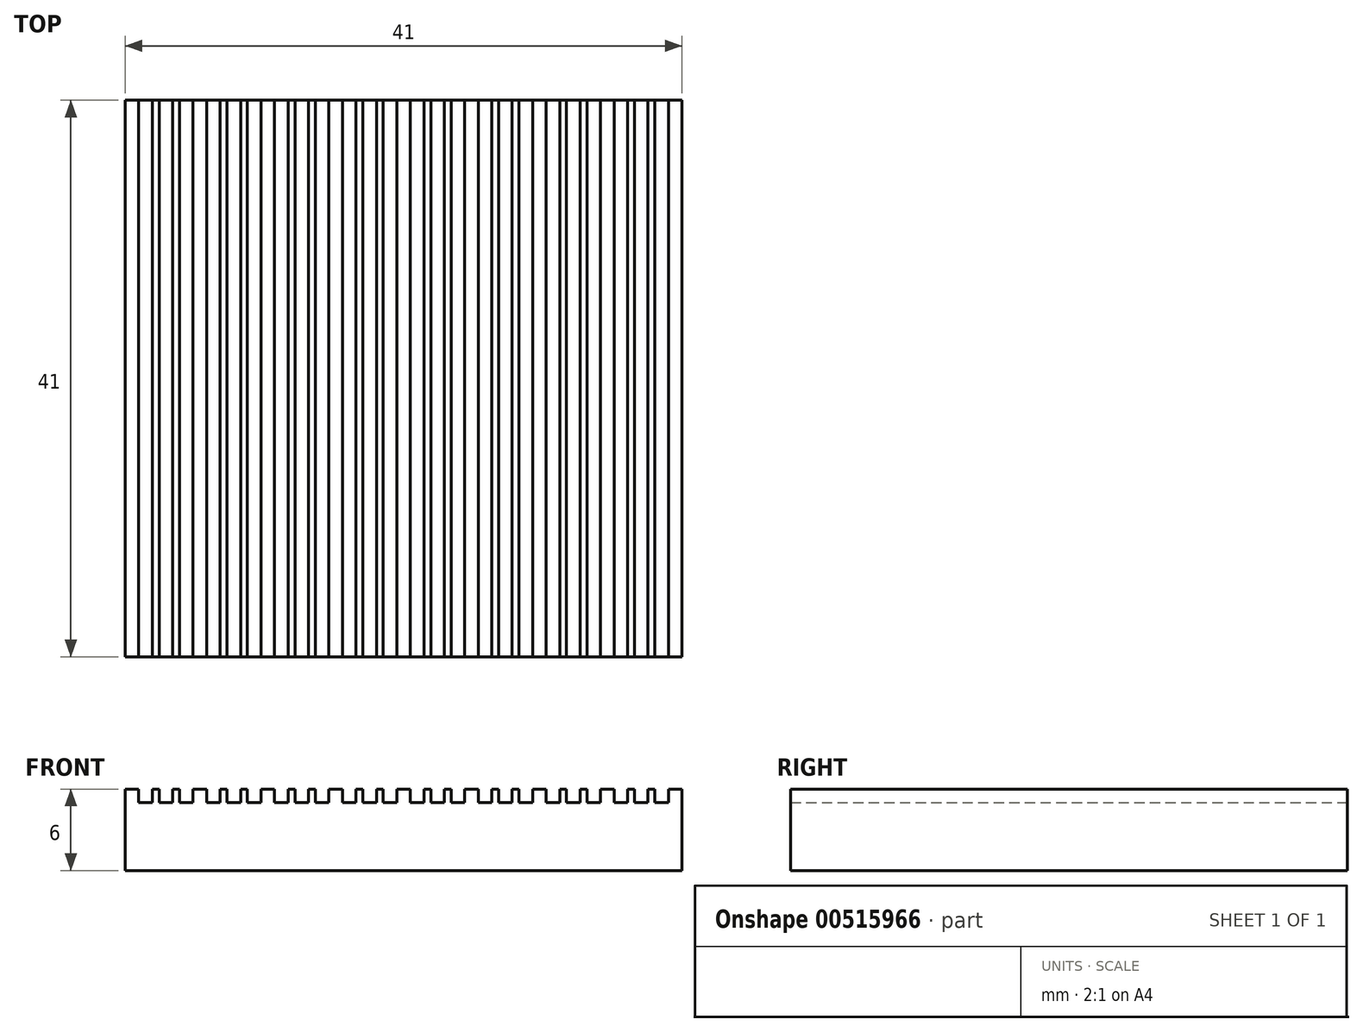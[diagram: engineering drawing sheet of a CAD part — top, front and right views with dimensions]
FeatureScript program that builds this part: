
annotation { "Feature Type Name" : "Feature", "Feature Type Description" : "" }
export const myFeature = defineFeature(function(context is Context, id is Id, definition is map)
    precondition{}
    {
        {
            var Q0;
            Q0=qCreatedBy(makeId("Front.planeOp"),FACE);
            var sketch = newSketch(context, id + "F0", { "sketchPlane" : qUnion([Q0])});
            skLineSegment(sketch, "E0", {"start": v(0, 6) * mm, "end": v(0, 0) * mm});
            skLineSegment(sketch, "E1", {"start": v(0, 0) * mm, "end": v(41, 0) * mm});
            skLineSegment(sketch, "E2", {"start": v(0, 6) * mm, "end": v(1, 6) * mm});
            skLineSegment(sketch, "E3", {"start": v(1, 6) * mm, "end": v(1, 5) * mm});
            skLineSegment(sketch, "E4", {"start": v(1, 5) * mm, "end": v(2, 5) * mm});
            skLineSegment(sketch, "E5", {"start": v(2, 5) * mm, "end": v(2, 6) * mm});
            skLineSegment(sketch, "E6", {"start": v(2, 6) * mm, "end": v(2.5, 6) * mm});
            skLineSegment(sketch, "E7", {"start": v(2.5, 6) * mm, "end": v(2.5, 5) * mm});
            skLineSegment(sketch, "E8", {"start": v(2.5, 5) * mm, "end": v(3.5, 5) * mm});
            skLineSegment(sketch, "E9", {"start": v(3.5, 5) * mm, "end": v(3.5, 6) * mm});
            skLineSegment(sketch, "E10", {"start": v(3.5, 6) * mm, "end": v(4, 6) * mm});
            skLineSegment(sketch, "E11", {"start": v(4, 6) * mm, "end": v(4, 5) * mm});
            skLineSegment(sketch, "E12", {"start": v(4, 5) * mm, "end": v(5, 5) * mm});
            skLineSegment(sketch, "E13", {"start": v(5, 5) * mm, "end": v(5, 6) * mm});
            skLineSegment(sketch, "E14.1.0.0", {"start": v(7.5, 6) * mm, "end": v(7.5, 5) * mm});
            skLineSegment(sketch, "E14.1.0.1", {"start": v(8.5, 5) * mm, "end": v(8.5, 6) * mm});
            skLineSegment(sketch, "E14.1.0.2", {"start": v(7.5, 5) * mm, "end": v(8.5, 5) * mm});
            skLineSegment(sketch, "E14.1.0.3", {"start": v(7, 5) * mm, "end": v(7, 6) * mm});
            skLineSegment(sketch, "E14.1.0.4", {"start": v(9, 6) * mm, "end": v(9, 5) * mm});
            skLineSegment(sketch, "E14.1.0.5", {"start": v(9, 5) * mm, "end": v(10, 5) * mm});
            skLineSegment(sketch, "E14.1.0.6", {"start": v(6, 5) * mm, "end": v(7, 5) * mm});
            skLineSegment(sketch, "E14.1.0.7", {"start": v(5, 6) * mm, "end": v(6, 6) * mm});
            skLineSegment(sketch, "E14.1.0.8", {"start": v(6, 6) * mm, "end": v(6, 5) * mm});
            skLineSegment(sketch, "E14.1.0.9", {"start": v(10, 5) * mm, "end": v(10, 6) * mm});
            skLineSegment(sketch, "E14.1.0.10", {"start": v(7, 6) * mm, "end": v(7.5, 6) * mm});
            skLineSegment(sketch, "E14.1.0.11", {"start": v(8.5, 6) * mm, "end": v(9, 6) * mm});
            skLineSegment(sketch, "E14.2.0.0", {"start": v(12.5, 6) * mm, "end": v(12.5, 5) * mm});
            skLineSegment(sketch, "E14.2.0.1", {"start": v(13.5, 5) * mm, "end": v(13.5, 6) * mm});
            skLineSegment(sketch, "E14.2.0.2", {"start": v(12.5, 5) * mm, "end": v(13.5, 5) * mm});
            skLineSegment(sketch, "E14.2.0.3", {"start": v(12, 5) * mm, "end": v(12, 6) * mm});
            skLineSegment(sketch, "E14.2.0.4", {"start": v(14, 6) * mm, "end": v(14, 5) * mm});
            skLineSegment(sketch, "E14.2.0.5", {"start": v(14, 5) * mm, "end": v(15, 5) * mm});
            skLineSegment(sketch, "E14.2.0.6", {"start": v(11, 5) * mm, "end": v(12, 5) * mm});
            skLineSegment(sketch, "E14.2.0.7", {"start": v(10, 6) * mm, "end": v(11, 6) * mm});
            skLineSegment(sketch, "E14.2.0.8", {"start": v(11, 6) * mm, "end": v(11, 5) * mm});
            skLineSegment(sketch, "E14.2.0.9", {"start": v(15, 5) * mm, "end": v(15, 6) * mm});
            skLineSegment(sketch, "E14.2.0.10", {"start": v(12, 6) * mm, "end": v(12.5, 6) * mm});
            skLineSegment(sketch, "E14.2.0.11", {"start": v(13.5, 6) * mm, "end": v(14, 6) * mm});
            skLineSegment(sketch, "E14.3.0.0", {"start": v(17.5, 6) * mm, "end": v(17.5, 5) * mm});
            skLineSegment(sketch, "E14.3.0.1", {"start": v(18.5, 5) * mm, "end": v(18.5, 6) * mm});
            skLineSegment(sketch, "E14.3.0.2", {"start": v(17.5, 5) * mm, "end": v(18.5, 5) * mm});
            skLineSegment(sketch, "E14.3.0.3", {"start": v(17, 5) * mm, "end": v(17, 6) * mm});
            skLineSegment(sketch, "E14.3.0.4", {"start": v(19, 6) * mm, "end": v(19, 5) * mm});
            skLineSegment(sketch, "E14.3.0.5", {"start": v(19, 5) * mm, "end": v(20, 5) * mm});
            skLineSegment(sketch, "E14.3.0.6", {"start": v(16, 5) * mm, "end": v(17, 5) * mm});
            skLineSegment(sketch, "E14.3.0.7", {"start": v(15, 6) * mm, "end": v(16, 6) * mm});
            skLineSegment(sketch, "E14.3.0.8", {"start": v(16, 6) * mm, "end": v(16, 5) * mm});
            skLineSegment(sketch, "E14.3.0.9", {"start": v(20, 5) * mm, "end": v(20, 6) * mm});
            skLineSegment(sketch, "E14.3.0.10", {"start": v(17, 6) * mm, "end": v(17.5, 6) * mm});
            skLineSegment(sketch, "E14.3.0.11", {"start": v(18.5, 6) * mm, "end": v(19, 6) * mm});
            skLineSegment(sketch, "E14.4.0.0", {"start": v(22.5, 6) * mm, "end": v(22.5, 5) * mm});
            skLineSegment(sketch, "E14.4.0.1", {"start": v(23.5, 5) * mm, "end": v(23.5, 6) * mm});
            skLineSegment(sketch, "E14.4.0.2", {"start": v(22.5, 5) * mm, "end": v(23.5, 5) * mm});
            skLineSegment(sketch, "E14.4.0.3", {"start": v(22, 5) * mm, "end": v(22, 6) * mm});
            skLineSegment(sketch, "E14.4.0.4", {"start": v(24, 6) * mm, "end": v(24, 5) * mm});
            skLineSegment(sketch, "E14.4.0.5", {"start": v(24, 5) * mm, "end": v(25, 5) * mm});
            skLineSegment(sketch, "E14.4.0.6", {"start": v(21, 5) * mm, "end": v(22, 5) * mm});
            skLineSegment(sketch, "E14.4.0.7", {"start": v(20, 6) * mm, "end": v(21, 6) * mm});
            skLineSegment(sketch, "E14.4.0.8", {"start": v(21, 6) * mm, "end": v(21, 5) * mm});
            skLineSegment(sketch, "E14.4.0.9", {"start": v(25, 5) * mm, "end": v(25, 6) * mm});
            skLineSegment(sketch, "E14.4.0.10", {"start": v(22, 6) * mm, "end": v(22.5, 6) * mm});
            skLineSegment(sketch, "E14.4.0.11", {"start": v(23.5, 6) * mm, "end": v(24, 6) * mm});
            skLineSegment(sketch, "E14.5.0.0", {"start": v(27.5, 6) * mm, "end": v(27.5, 5) * mm});
            skLineSegment(sketch, "E14.5.0.1", {"start": v(28.5, 5) * mm, "end": v(28.5, 6) * mm});
            skLineSegment(sketch, "E14.5.0.2", {"start": v(27.5, 5) * mm, "end": v(28.5, 5) * mm});
            skLineSegment(sketch, "E14.5.0.3", {"start": v(27, 5) * mm, "end": v(27, 6) * mm});
            skLineSegment(sketch, "E14.5.0.4", {"start": v(29, 6) * mm, "end": v(29, 5) * mm});
            skLineSegment(sketch, "E14.5.0.5", {"start": v(29, 5) * mm, "end": v(30, 5) * mm});
            skLineSegment(sketch, "E14.5.0.6", {"start": v(26, 5) * mm, "end": v(27, 5) * mm});
            skLineSegment(sketch, "E14.5.0.7", {"start": v(25, 6) * mm, "end": v(26, 6) * mm});
            skLineSegment(sketch, "E14.5.0.8", {"start": v(26, 6) * mm, "end": v(26, 5) * mm});
            skLineSegment(sketch, "E14.5.0.9", {"start": v(30, 5) * mm, "end": v(30, 6) * mm});
            skLineSegment(sketch, "E14.5.0.10", {"start": v(27, 6) * mm, "end": v(27.5, 6) * mm});
            skLineSegment(sketch, "E14.5.0.11", {"start": v(28.5, 6) * mm, "end": v(29, 6) * mm});
            skLineSegment(sketch, "E14.6.0.0", {"start": v(32.5, 6) * mm, "end": v(32.5, 5) * mm});
            skLineSegment(sketch, "E14.6.0.1", {"start": v(33.5, 5) * mm, "end": v(33.5, 6) * mm});
            skLineSegment(sketch, "E14.6.0.2", {"start": v(32.5, 5) * mm, "end": v(33.5, 5) * mm});
            skLineSegment(sketch, "E14.6.0.3", {"start": v(32, 5) * mm, "end": v(32, 6) * mm});
            skLineSegment(sketch, "E14.6.0.4", {"start": v(34, 6) * mm, "end": v(34, 5) * mm});
            skLineSegment(sketch, "E14.6.0.5", {"start": v(34, 5) * mm, "end": v(35, 5) * mm});
            skLineSegment(sketch, "E14.6.0.6", {"start": v(31, 5) * mm, "end": v(32, 5) * mm});
            skLineSegment(sketch, "E14.6.0.7", {"start": v(30, 6) * mm, "end": v(31, 6) * mm});
            skLineSegment(sketch, "E14.6.0.8", {"start": v(31, 6) * mm, "end": v(31, 5) * mm});
            skLineSegment(sketch, "E14.6.0.9", {"start": v(35, 5) * mm, "end": v(35, 6) * mm});
            skLineSegment(sketch, "E14.6.0.10", {"start": v(32, 6) * mm, "end": v(32.5, 6) * mm});
            skLineSegment(sketch, "E14.6.0.11", {"start": v(33.5, 6) * mm, "end": v(34, 6) * mm});
            skLineSegment(sketch, "E14.7.0.0", {"start": v(37.5, 6) * mm, "end": v(37.5, 5) * mm});
            skLineSegment(sketch, "E14.7.0.1", {"start": v(38.5, 5) * mm, "end": v(38.5, 6) * mm});
            skLineSegment(sketch, "E14.7.0.2", {"start": v(37.5, 5) * mm, "end": v(38.5, 5) * mm});
            skLineSegment(sketch, "E14.7.0.3", {"start": v(37, 5) * mm, "end": v(37, 6) * mm});
            skLineSegment(sketch, "E14.7.0.4", {"start": v(39, 6) * mm, "end": v(39, 5) * mm});
            skLineSegment(sketch, "E14.7.0.5", {"start": v(39, 5) * mm, "end": v(40, 5) * mm});
            skLineSegment(sketch, "E14.7.0.6", {"start": v(36, 5) * mm, "end": v(37, 5) * mm});
            skLineSegment(sketch, "E14.7.0.7", {"start": v(35, 6) * mm, "end": v(36, 6) * mm});
            skLineSegment(sketch, "E14.7.0.8", {"start": v(36, 6) * mm, "end": v(36, 5) * mm});
            skLineSegment(sketch, "E14.7.0.9", {"start": v(40, 5) * mm, "end": v(40, 6) * mm});
            skLineSegment(sketch, "E14.7.0.10", {"start": v(37, 6) * mm, "end": v(37.5, 6) * mm});
            skLineSegment(sketch, "E14.7.0.11", {"start": v(38.5, 6) * mm, "end": v(39, 6) * mm});
            skLineSegment(sketch, "E14.direction1", {"start": v(1, 5) * mm, "end": v(6, 5) * mm, "construction": true});
            skLineSegment(sketch, "E15", {"start": v(41, 0) * mm, "end": v(41, 6) * mm});
            skLineSegment(sketch, "E16", {"start": v(41, 6) * mm, "end": v(40, 6) * mm});
            skSolve(sketch);
        }
        {
            var Q0;
            Q0 = qSketchRegion(id + "F0", true);
            extrude(context, id + "F1", {"entities" : qUnion([Q0]), "depth" : 41 * mm, "offsetDistance" : 25 * mm});
        }
    });
